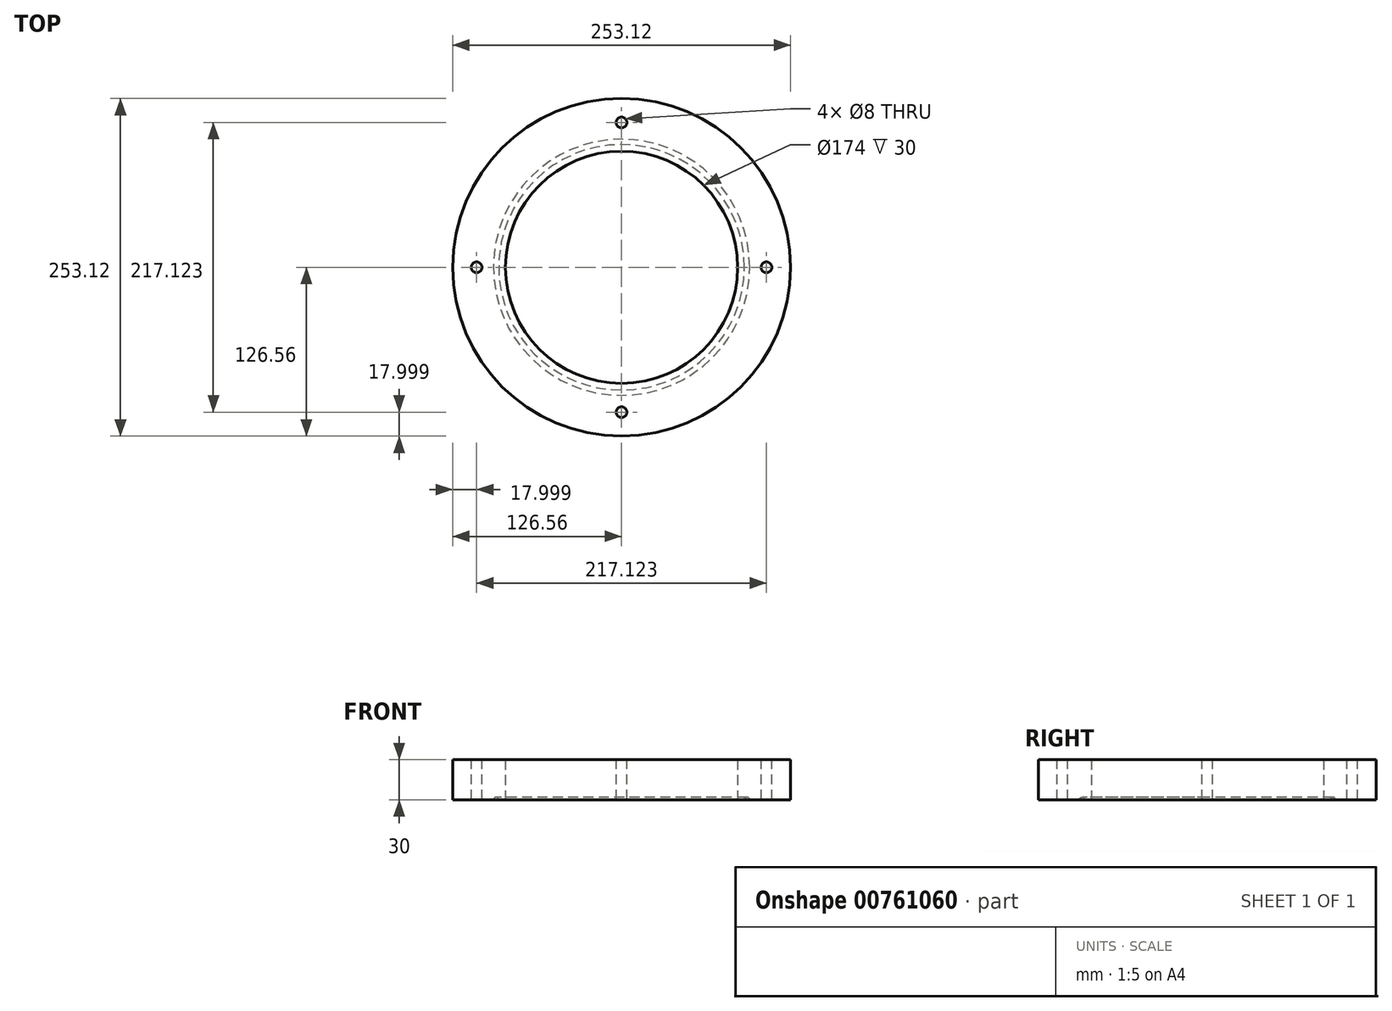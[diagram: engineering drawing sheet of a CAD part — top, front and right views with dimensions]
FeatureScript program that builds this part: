
annotation { "Feature Type Name" : "Feature", "Feature Type Description" : "" }
export const myFeature = defineFeature(function(context is Context, id is Id, definition is map)
    precondition{}
    {
        {
            var Q0;
            Q0=qCreatedBy(makeId("Front.planeOp"),FACE);
            var sketch = newSketch(context, id + "F0", { "sketchPlane" : qUnion([Q0])});
            skLineSegment(sketch, "E0", {"start": v(87, 0) * mm, "end": v(87, 30) * mm});
            skLineSegment(sketch, "E1", {"start": v(87, 0) * mm, "end": v(92, 0) * mm});
            skLineSegment(sketch, "E2", {"start": v(95.99, 0) * mm, "end": v(126.56, 0) * mm});
            skLineSegment(sketch, "E3", {"start": v(126.56, 0) * mm, "end": v(126.56, 30) * mm});
            skLineSegment(sketch, "E4", {"start": v(126.56, 30) * mm, "end": v(87, 30) * mm});
            skArc(sketch, "E5", {"start": v(95.99, 0) * mm, "mid": v(94, 1.85) * mm, "end": v(92, 0) * mm});
            skLineSegment(sketch, "E6", {"start": v(0, -67.7) * mm, "end": v(0, 74.86) * mm});
            skSolve(sketch);
        }
        {
            var Q0;
            Q0 = qSketchRegion(id + "F0", true);
            var Q1;
            Q1=sQuery(id+"F0.wireOp",EDGE,"E6");
            revolve(context, id + "F1", {"surfaceOperationType" : NewSurfaceOperationType.NEW, "entities" : qUnion([Q0]), "axis" : qUnion([Q1]), "revolveType" : RevolveType.FULL});
        }
        {
            var Q0;
            Q0=makeQuery(id+"F1.opRevolve","SWEPT_FACE",FACE,{"disambiguationData":[OSD([sQuery(id+"F0.wireOp",EDGE,"E4")])]});
            var sketch = newSketch(context, id + "F2", { "sketchPlane" : qUnion([Q0])});
            skCircle(sketch, "E7", {"center": v(108.56, 0) * mm, "radius": 4 * mm});
            skCircle(sketch, "E8", {"center": v(0, 108.56) * mm, "radius": 4 * mm});
            skCircle(sketch, "E9", {"center": v(-108.56, 0) * mm, "radius": 4 * mm});
            skCircle(sketch, "E10", {"center": v(0, -108.56) * mm, "radius": 4 * mm});
            skSolve(sketch);
        }
        {
            var Q0;
            Q0 = qSketchRegion(id + "F2", true);
            extrude(context, id + "F3", {"entities" : qUnion([Q0]), "operationType" : NewBodyOperationType.REMOVE, "endBound" : BoundingType.THROUGH_ALL, "oppositeDirection" : true, "depth" : 25 * mm, "offsetDistance" : 25 * mm});
        }
    });
